# Revit family: Kessel 8740141 en
name_source: partatom
category: Sanitärinstallationen
revit_build: Autodesk Revit 2017 (Build: 20160225_1515(x64)
units: mm (PartAtom-declared; Revit-internal decimal feet)

## family parameters
Arbeitsebenenbasiert = Nein
Beim Laden mit Abzugskörper schneiden = Nein
Bemaßung runder Anschluss = Durchmesser verwenden
Gemeinsam genutzt = Nein
Immer vertikal = Ja
Raumberechnungspunkt = Nein
Teiletyp = Normal

## types (1)
- Kessel 8740141 en
    <1.010.00.2> Number of the part of the guideline = 38
    <1.010.00.3> Issue date (month) of the guideline = 201805
    <1.010.00.4> Manufacturer name = Kessel
    <1.010.00.5> Revision date of the file = 20190228
    <1.800.00.3> BS number = 1060010000000000000000000000000000000000000000010900000000
    <1.800.00.4> Comment field = Schachtmodul LW 1000 Erdeinbau, Zugang LW 800, 620-869 mm, Klasse B
    <1.810.00.3> Manufacturer’s reference number = 8740141
    <1.810.00.4> DATANORM number = 8740141
    <1.810.00.6> GTIN number = 4026092070079
    <1.960/3L.00.8> Link (URL) = http://www.kessel.de
    <38.100.00.4> Drain type for floor, roof and sanitary objects = Zubehör Rückstauverschlüsse
    <38.110.00.4> Floor, roof and sanitary works sequences = Zubehör
    <38.700.00.10> Type of rated / operating voltage = 0
    <38.700.00.15> Connection to GLT, GA = no
    <38.700.00.16> Fire resistance class can be retrofitted = no
    <38.700.00.4> product name = Schachtmodul LW 1000 Erdeinbau, Zugang LW 800, 620-869 mm, Klasse B
    <38.700.00.6> Complete article (one-piece) from combination (multi-part design) Drain body and attachment piece = no
    <38.700.00.7> Potential compensation (ground connection) available = no
    <38.700.00.8> Electrical connection = no
    CONNECTOR0_DIAMETER_dX_0r = 0 mm  [stored 0 ft]
    CONNECTOR0_dX_00 = 501 mm
    CONNECTOR0_dX_01 = 500 mm  [stored 1.64042 ft]
    CONNECTOR0_ref_dX = 501 mm
    CONNECTOR0_ref_dZ = 206 mm
    CONNECTOR1_DIAMETER_dY_0r = 0 mm  [stored 0 ft]
    CONNECTOR1_dY_00 = 500 mm  [stored 1.64042 ft]
    CONNECTOR1_dY_01 = 501 mm
    CONNECTOR1_ref_dY = 501 mm
    CONNECTOR1_ref_dZ = 206 mm
    CONNECTOR2_DIAMETER_dZ_0r = 0 mm  [stored 0 ft]
    CONNECTOR2_dZ_00 = 1 mm  [stored 0.00328084 ft]
    CONNECTOR2_ref_dZ = 1 mm  [stored 0.00328084 ft]
    Hersteller = Kessel
    Modell = 8740141
    URL = www.kessel.de

note: [stored X ft] marks values corroborated as IEEE doubles in the binary element streams (Revit-internal decimal feet)

## geometry (parser evidence)
native form markers: Sweep x2
no freeform markers — native parametric forms only
